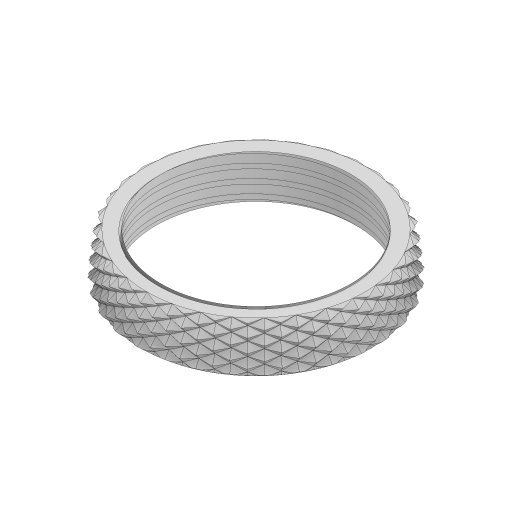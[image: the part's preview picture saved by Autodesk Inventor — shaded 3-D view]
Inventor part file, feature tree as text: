
AUTODESK INVENTOR PART (.ipt)
format: ipt  version: 2023 (Build 270158000, 158)  size: 4,270,592 bytes
history: native  units: mm
features: sketch x5, helix x3, draft x2, extrude x1, pattern_circular x1, mirror x1, revolve x1, projected_geometry x1
ambient origin geometry x8: Origin, YZ Plane, XZ Plane, XY Plane, X Axis, Y Axis, Z Axis, Center Point
bodies: Solid1 (feature_tree)
feature tree (15):
  extrude  "Extrusion1"  Depth=6.52mm TaperAngle=0.0deg
  draft  "FaceDraft1"
  sketch  "Sketch2"  dims[d7=2.0mm d8=9.0mm d9=10.0mm d10=1.047198mm d11=90.0deg d12=90.0deg d13=0.0mm d14=0.0mm d15=2.0mm d16=3.0mm d17=10.0mm d18=-1.047198mm d19=90.0deg d20=90.0deg d21=0.0mm d22=0.0mm d23=3.5mm d91=1.047198mm d109=2.094395mm]
  sketch  "Sketch4"  dims[d112=2.0mm d113=6.52mm d114=1.25mm d115=1.047198mm]
  helix  "Coil1"  [1 undecoded]
  helix  "Coil2"  [1 undecoded]
  draft  "FaceDraft2"
  helix  "Coil10"  [1 undecoded]
  pattern_circular  "Circular Pattern5"  Count=30 Angle=360.0deg
  mirror  "Mirror1"
  revolve  "Revolution2"  [1 undecoded]
  sketch  "Sketch1"  dims[d0=26.5mm d2=6.52mm d3=0.0mm d4=1.047198mm]
  sketch  "Sketch13"  dims[d116=90.0deg d117=90.0deg d118=0.0mm d119=0.0mm d122=300.0mm d123=360.0deg]
  sketch  "Sketch14"  dims[d127=60.0deg d128=15.211695mm d129=360.0deg d130=8.726646mm]
  projected_geometry  "Project Cut Edges1"
note: 4 required parameter values undecoded (feature->parameter linkage not recoverable at this tier; creation-order binding heuristic only, values carry confidence <= 0.55)